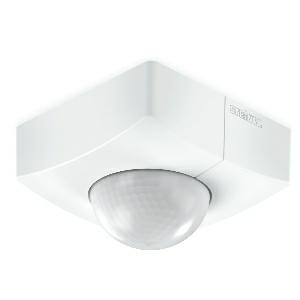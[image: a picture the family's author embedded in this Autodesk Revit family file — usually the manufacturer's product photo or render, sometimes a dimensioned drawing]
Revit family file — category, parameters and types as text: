
# Revit family: is_345_mx_highbay_010522
name_source: partatom
category: Elektroinstallationen
revit_build: Autodesk Revit 2016 (Build: 20190508_0715(x64)
units: mm (PartAtom-declared; Revit-internal decimal feet)

## family parameters
Basisbauteil = Fläche
Beim Laden mit Abzugskörper schneiden = Nein
Bemaßung runder Anschluss = Durchmesser verwenden
Beschriftungsausrichtung beibehalten = Nein
Gemeinsam genutzt = Nein
Raumberechnungspunkt = Nein
Teiletyp = Normal

## types (1)
- IS 345 MX Highbay
    Apparent Load = 0 VA
    Beschreibung = Type: Motion detectors; Dimensions (L x W x H): 65 x 95 x 95 mm; Mains power supply: 220 – 240 V / 50 – 60 Hz; Sensor Technology: passive infrared; Application, place: Indoors; Application, room: high-bay warehouse, Indoors; Installation site: ceiling; Installation: Surface wiring; Switching zones: 280 switching zones; Electronic scalability: No; Mechanical scalability: No; Mounting height: 4,00 – 14,00 m; Optimum mounting height: 12 m; Detection angle: 360 °; Angle of aperture: 9 °; Sneak-by guard: Yes; Capability of masking out individual segments: Yes; Reach, radial: 30 x 4 m (120 m²); Reach, tangential: 30 x 4 m (120 m²); Twilight setting TEACH: Yes; Twilight setting: 2 – 1000 lx; Time setting: 5 sec – 15 min; Constant-lighting control: No; Basic light level function: No; Functions: Normal / test mode, Manual ON / ON-OFF; Settings via: Remote control, Potentiometers, Smart Remote; With remote control: No; Interconnection: Yes; IP-rating: IP54; Material: Plastic; Ambient temperature: -20 – 50 °C; Colour: white; Colour, RAL: 9003; Manufacturer's Warranty: 5 years; Version: PF - surface, sq.; PU1, EAN: 4007841010522
    Height = 95 mm
    Hersteller = Steinel
    Length = 65 mm
    Maximum range = 3.441 m
    ModVariant = Nein
    Modell = 010522
    Mounting Place = Ceiling
    Mounting Type = Surface mounted
    Number of Poles = 1
    OnlyDefault = Ja
    Power Factor = 1
    Product Name = IS 345 MX Highbay
    Product group = Sensor-switched outdoor light
    ProductGroupID = 3
    Protection Class = Protection class
    Protection Degree = IP 54
    RlxData = <blob elided: 194589 chars, md5=f9460267>
    Sensor characteristics = Circular 300°-360°
    Sensor type = Passive (infrared)
    SensorDataFile = <blob elided: 170895 chars, md5=da062800>
    Type of entry = Motion
    Typenbild = produkt1_010522.jpg
    Typenkommentare = Product without accessories
    URL = http://relux.com
    VarID = ---
    Voltage = 0 V
    Vorgabe-Ansicht = 1800 mm
    Weight = 0.00 kg
    Width = 95 mm

## geometry (parser evidence)
native form markers: Sweep x16
no freeform markers — native parametric forms only
